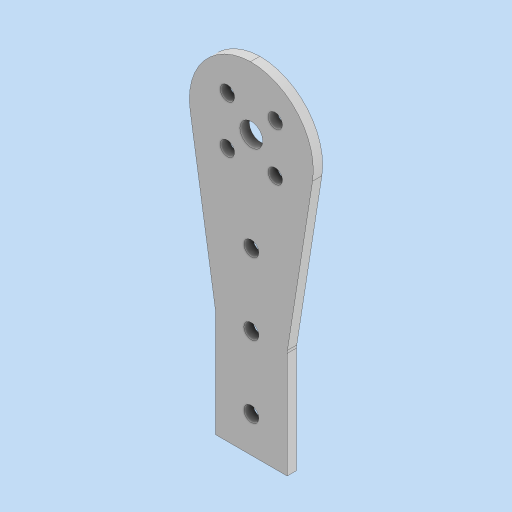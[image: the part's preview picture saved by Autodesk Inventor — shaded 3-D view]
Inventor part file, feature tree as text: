
AUTODESK INVENTOR PART (.ipt)
format: ipt  version: 2024 (Build 280153000, 153)  size: 246,272 bytes
history: native  units: in
note: dims shown in document units (in); Inventor stores cm internally (conversion verified against a paired STEP export)
features: fillet x5, sketch x2, extrude x1, hole x1, pattern_circular x1
ambient origin geometry x8: Origin, YZ Plane, XZ Plane, XY Plane, X Axis, Y Axis, Z Axis, Center Point
bodies: Solid1 (feature_tree)
feature tree (10):
  extrude  "Extrusion1"  Depth=0.875in
  fillet  "Fillet9"  Radius=0.209in
  fillet  "Fillet10"  Radius=0.209in
  fillet  "Fillet11"  Radius=0.875in
  fillet  "Fillet12"  Radius=0.875in
  hole  "Hole1"  [1 undecoded]
  pattern_circular  "Circular Pattern2"  [2 undecoded]
  fillet  "Fillet15"  Radius=0.5in
  sketch  "Sketch1"  dims[d0=1.75in d2=0.3189in d3=0.209in d4=0.209in d5=0.875in d8=0.875in]
  sketch  "Sketch3"  dims[d9=0.875in d10=0.13in d11=0.0in d20=0.5in d21=0.5in d22=0.875in d23=0.875in d26=1.2598in d27=0.6299in d28=0.9449in d29=0.201in d30=0.75in d31=0.37in d32=0.25in d33=90.0deg d34=0.559in d35=0.8108in d40=45.0deg d41=1.5748in d42=360.0deg d44=0.209in d47=0.25in d50=90.0deg d51=1.375in d53=0.5in d54=1.0in d55=1.0in d56=0.0in d16=0.0in d17=0.0in d18=0.0in d19=0.0in]
note: 3 required parameter values undecoded (feature->parameter linkage not recoverable at this tier; creation-order binding heuristic only, values carry confidence <= 0.55)
